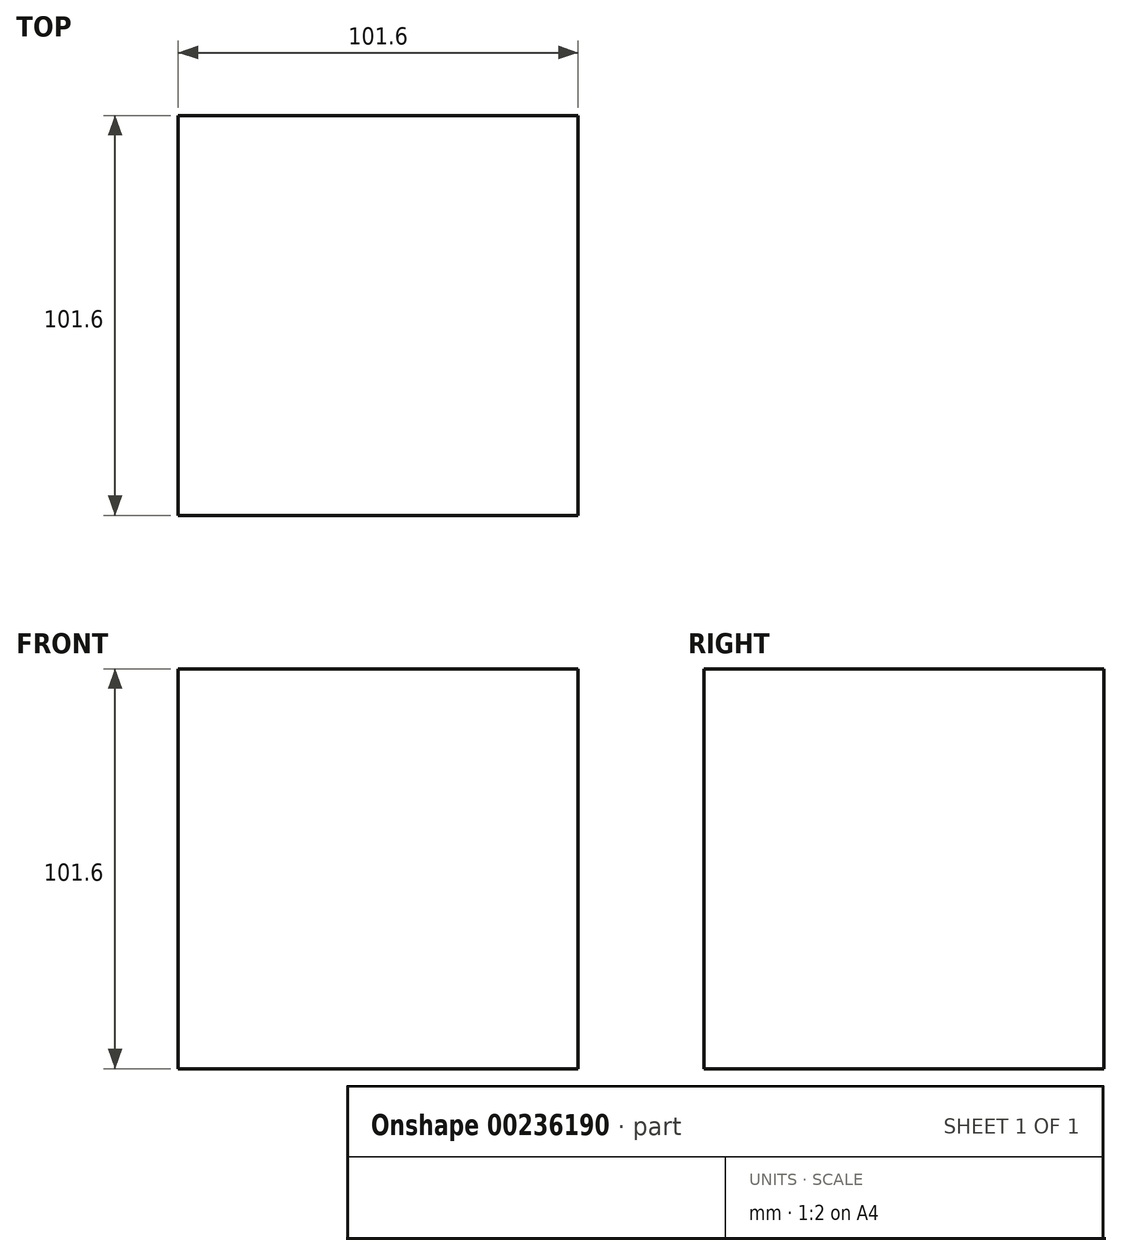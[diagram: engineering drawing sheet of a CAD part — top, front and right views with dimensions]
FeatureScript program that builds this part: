
annotation { "Feature Type Name" : "Feature", "Feature Type Description" : "" }
export const myFeature = defineFeature(function(context is Context, id is Id, definition is map)
    precondition{}
    {
        {
            var Q0;
            Q0=qCreatedBy(makeId("Front.planeOp"),FACE);
            var sketch = newSketch(context, id + "F0", { "sketchPlane" : qUnion([Q0])});
            skLineSegment(sketch, "E0.bottom", {"start": v(-50.61, 53.43) * mm, "end": v(50.99, 53.43) * mm});
            skLineSegment(sketch, "E0.top", {"start": v(-50.61, -48.17) * mm, "end": v(50.99, -48.17) * mm});
            skLineSegment(sketch, "E0.left", {"start": v(-50.61, 53.43) * mm, "end": v(-50.61, -48.17) * mm});
            skLineSegment(sketch, "E0.right", {"start": v(50.99, 53.43) * mm, "end": v(50.99, -48.17) * mm});
            skSolve(sketch);
        }
        {
            var Q0;
            Q0 = qSketchRegion(id + "F0", true);
            extrude(context, id + "F1", {"entities" : qUnion([Q0]), "depth" : 101.6 * mm});
        }
    });
